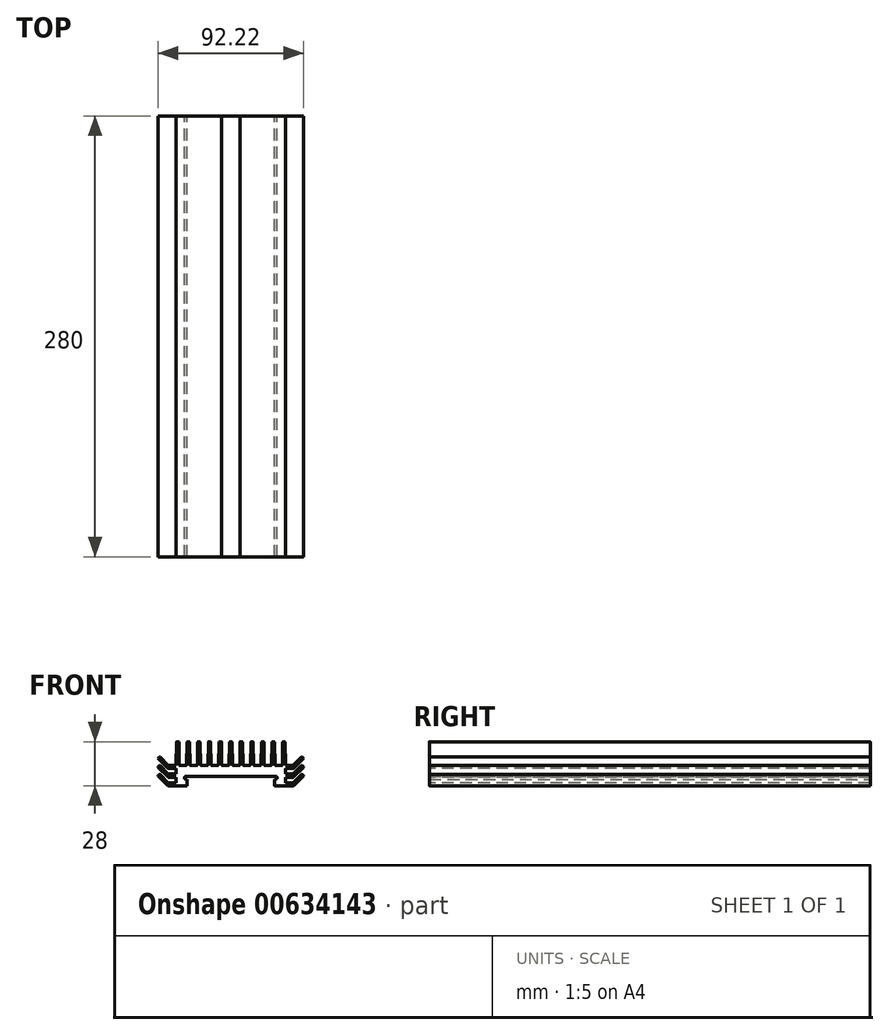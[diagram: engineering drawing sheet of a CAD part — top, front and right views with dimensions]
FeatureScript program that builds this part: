
annotation { "Feature Type Name" : "Feature", "Feature Type Description" : "" }
export const myFeature = defineFeature(function(context is Context, id is Id, definition is map)
    precondition{}
    {
        {
            var Q0;
            Q0=qCreatedBy(makeId("Front.planeOp"),FACE);
            var sketch = newSketch(context, id + "F0", { "sketchPlane" : qUnion([Q0])});
            skLineSegment(sketch, "E0.1.0.0", {"start": v(-33, 18.3) * mm, "end": v(-32.75, 3.7) * mm});
            skLineSegment(sketch, "E0.1.0.1", {"start": v(-32.55, 3.5) * mm, "end": v(-28.2, 3.5) * mm});
            skLineSegment(sketch, "E0.1.0.2", {"start": v(-34.75, 3.77) * mm, "end": v(-34.5, 18.3) * mm});
            skLineSegment(sketch, "E0.1.0.3", {"start": v(-34.3, 18.5) * mm, "end": v(-33.2, 18.5) * mm});
            skLineSegment(sketch, "E0.2.0.0", {"start": v(-26.25, 18.3) * mm, "end": v(-26, 3.7) * mm});
            skLineSegment(sketch, "E0.2.0.1", {"start": v(-25.8, 3.5) * mm, "end": v(-21.45, 3.5) * mm});
            skLineSegment(sketch, "E0.2.0.2", {"start": v(-28, 3.7) * mm, "end": v(-27.75, 18.3) * mm});
            skLineSegment(sketch, "E0.2.0.3", {"start": v(-27.55, 18.5) * mm, "end": v(-26.45, 18.5) * mm});
            skLineSegment(sketch, "E0.3.0.0", {"start": v(-19.5, 18.3) * mm, "end": v(-19.25, 3.7) * mm});
            skLineSegment(sketch, "E0.3.0.1", {"start": v(-19.05, 3.5) * mm, "end": v(-14.7, 3.5) * mm});
            skLineSegment(sketch, "E0.3.0.2", {"start": v(-21.25, 3.7) * mm, "end": v(-21, 18.3) * mm});
            skLineSegment(sketch, "E0.3.0.3", {"start": v(-20.8, 18.5) * mm, "end": v(-19.7, 18.5) * mm});
            skLineSegment(sketch, "E0.4.0.0", {"start": v(-12.75, 18.3) * mm, "end": v(-12.5, 3.7) * mm});
            skLineSegment(sketch, "E0.4.0.1", {"start": v(-12.3, 3.5) * mm, "end": v(-7.95, 3.5) * mm});
            skLineSegment(sketch, "E0.4.0.2", {"start": v(-14.5, 3.7) * mm, "end": v(-14.25, 18.3) * mm});
            skLineSegment(sketch, "E0.4.0.3", {"start": v(-14.05, 18.5) * mm, "end": v(-12.95, 18.5) * mm});
            skLineSegment(sketch, "E0.5.0.0", {"start": v(-5.75, 18.3) * mm, "end": v(-5.75, 3.7) * mm});
            skLineSegment(sketch, "E0.5.0.1", {"start": v(-5.55, 3.5) * mm, "end": v(-1.2, 3.5) * mm});
            skLineSegment(sketch, "E0.5.0.2", {"start": v(-7.75, 3.7) * mm, "end": v(-7.5, 18.3) * mm});
            skLineSegment(sketch, "E0.5.0.3", {"start": v(-7.3, 18.5) * mm, "end": v(-5.95, 18.5) * mm});
            skLineSegment(sketch, "E1.6.6.0", {"start": v(-1, 3.7) * mm, "end": v(-0.75, 18.3) * mm});
            skLineSegment(sketch, "E1.9.6.0", {"start": v(-0.55, 18.5) * mm, "end": v(0, 18.5) * mm});
            skPoint(sketch, "E2", {"position": v(0, 18.5) * mm});
            skPoint(sketch, "E3.visualSharp", {"position": v(-34.5, 18.5) * mm});
            skArc(sketch, "E3.filletArc", {"start": v(-34.3, 18.5) * mm, "mid": v(-34.44, 18.44) * mm, "end": v(-34.5, 18.3) * mm});
            skPoint(sketch, "E4.visualSharp", {"position": v(-33, 18.5) * mm});
            skArc(sketch, "E4.filletArc", {"start": v(-33, 18.3) * mm, "mid": v(-33.06, 18.44) * mm, "end": v(-33.2, 18.5) * mm});
            skPoint(sketch, "E5.visualSharp", {"position": v(-27.75, 18.5) * mm});
            skArc(sketch, "E5.filletArc", {"start": v(-27.55, 18.5) * mm, "mid": v(-27.7, 18.44) * mm, "end": v(-27.75, 18.3) * mm});
            skPoint(sketch, "E6.visualSharp", {"position": v(-26.25, 18.5) * mm});
            skArc(sketch, "E6.filletArc", {"start": v(-26.25, 18.3) * mm, "mid": v(-26.3, 18.44) * mm, "end": v(-26.45, 18.5) * mm});
            skPoint(sketch, "E7.visualSharp", {"position": v(-21, 18.5) * mm});
            skArc(sketch, "E7.filletArc", {"start": v(-20.8, 18.5) * mm, "mid": v(-20.94, 18.44) * mm, "end": v(-21, 18.3) * mm});
            skPoint(sketch, "E8.visualSharp", {"position": v(-19.5, 18.5) * mm});
            skArc(sketch, "E8.filletArc", {"start": v(-19.5, 18.3) * mm, "mid": v(-19.56, 18.44) * mm, "end": v(-19.7, 18.5) * mm});
            skPoint(sketch, "E9.visualSharp", {"position": v(-14.25, 18.5) * mm});
            skArc(sketch, "E9.filletArc", {"start": v(-14.05, 18.5) * mm, "mid": v(-14.2, 18.44) * mm, "end": v(-14.25, 18.3) * mm});
            skPoint(sketch, "E10.visualSharp", {"position": v(-12.75, 18.5) * mm});
            skArc(sketch, "E10.filletArc", {"start": v(-12.75, 18.3) * mm, "mid": v(-12.8, 18.44) * mm, "end": v(-12.95, 18.5) * mm});
            skPoint(sketch, "E11.visualSharp", {"position": v(-7.5, 18.5) * mm});
            skArc(sketch, "E11.filletArc", {"start": v(-7.3, 18.5) * mm, "mid": v(-7.44, 18.44) * mm, "end": v(-7.5, 18.3) * mm});
            skPoint(sketch, "E12.visualSharp", {"position": v(-5.75, 18.5) * mm});
            skArc(sketch, "E12.filletArc", {"start": v(-5.75, 18.3) * mm, "mid": v(-5.8, 18.44) * mm, "end": v(-5.95, 18.5) * mm});
            skPoint(sketch, "E13.visualSharp", {"position": v(-0.75, 18.5) * mm});
            skArc(sketch, "E13.filletArc", {"start": v(-0.55, 18.5) * mm, "mid": v(-0.7, 18.44) * mm, "end": v(-0.75, 18.3) * mm});
            skPoint(sketch, "E14.visualSharp", {"position": v(0, -3.5) * mm});
            skPoint(sketch, "E15.visualSharp", {"position": v(-32.75, 3.5) * mm});
            skArc(sketch, "E15.filletArc", {"start": v(-32.75, 3.7) * mm, "mid": v(-32.7, 3.56) * mm, "end": v(-32.55, 3.5) * mm});
            skPoint(sketch, "E16.visualSharp", {"position": v(-28, 3.5) * mm});
            skArc(sketch, "E16.filletArc", {"start": v(-28.2, 3.5) * mm, "mid": v(-28.06, 3.56) * mm, "end": v(-28, 3.7) * mm});
            skPoint(sketch, "E17.visualSharp", {"position": v(-26, 3.5) * mm});
            skArc(sketch, "E17.filletArc", {"start": v(-26, 3.7) * mm, "mid": v(-25.94, 3.56) * mm, "end": v(-25.8, 3.5) * mm});
            skPoint(sketch, "E18.visualSharp", {"position": v(-21.25, 3.5) * mm});
            skArc(sketch, "E18.filletArc", {"start": v(-21.45, 3.5) * mm, "mid": v(-21.3, 3.56) * mm, "end": v(-21.25, 3.7) * mm});
            skPoint(sketch, "E19.visualSharp", {"position": v(-19.25, 3.5) * mm});
            skArc(sketch, "E19.filletArc", {"start": v(-19.25, 3.7) * mm, "mid": v(-19.2, 3.56) * mm, "end": v(-19.05, 3.5) * mm});
            skPoint(sketch, "E20.visualSharp", {"position": v(-14.5, 3.5) * mm});
            skArc(sketch, "E20.filletArc", {"start": v(-14.7, 3.5) * mm, "mid": v(-14.56, 3.56) * mm, "end": v(-14.5, 3.7) * mm});
            skPoint(sketch, "E21.visualSharp", {"position": v(-12.5, 3.5) * mm});
            skArc(sketch, "E21.filletArc", {"start": v(-12.5, 3.7) * mm, "mid": v(-12.44, 3.56) * mm, "end": v(-12.3, 3.5) * mm});
            skPoint(sketch, "E22.visualSharp", {"position": v(-7.75, 3.5) * mm});
            skArc(sketch, "E22.filletArc", {"start": v(-7.95, 3.5) * mm, "mid": v(-7.8, 3.56) * mm, "end": v(-7.75, 3.7) * mm});
            skPoint(sketch, "E23.visualSharp", {"position": v(-5.75, 3.5) * mm});
            skArc(sketch, "E23.filletArc", {"start": v(-5.75, 3.7) * mm, "mid": v(-5.7, 3.56) * mm, "end": v(-5.55, 3.5) * mm});
            skPoint(sketch, "E24.visualSharp", {"position": v(-1, 3.5) * mm});
            skArc(sketch, "E24.filletArc", {"start": v(-1.2, 3.5) * mm, "mid": v(-1.06, 3.56) * mm, "end": v(-1, 3.7) * mm});
            skLineSegment(sketch, "E25", {"start": v(-27.75, -5.25) * mm, "end": v(-27.75, -9.3) * mm});
            skPoint(sketch, "E26.visualSharp", {"position": v(-27.75, -9.5) * mm});
            skArc(sketch, "E26.filletArc", {"start": v(-27.95, -9.5) * mm, "mid": v(-27.8, -9.44) * mm, "end": v(-27.75, -9.3) * mm});
            skLineSegment(sketch, "E27", {"start": v(-34.75, 3.77) * mm, "end": v(-34.75, -9.5) * mm});
            skLineSegment(sketch, "E28", {"start": v(-27.95, -9.5) * mm, "end": v(-34.75, -9.5) * mm});
            skLineSegment(sketch, "E29", {"start": v(0, 18.5) * mm, "end": v(0, -3.5) * mm});
            skLineSegment(sketch, "E30.bottom", {"start": v(-27.75, -5.25) * mm, "end": v(-28.62, -5.25) * mm});
            skArc(sketch, "E31", {"start": v(-28.62, -3.5) * mm, "mid": v(-29.5, -4.38) * mm, "end": v(-28.62, -5.25) * mm});
            skPoint(sketch, "E32", {"position": v(-29.5, -4.38) * mm});
            skLineSegment(sketch, "E33", {"start": v(-28.62, -3.5) * mm, "end": v(0, -3.5) * mm});
            skSolve(sketch);
        }
        {
            var Q0;
            Q0=qSketchRegion(id+"F0",true);
            extrude(context, id + "F1", {"entities" : qUnion([Q0]), "depth" : 280 * mm, "offsetDistance" : 25 * mm});
        }
        {
            var Q0;
            Q0=makeQuery(id+"F1.opExtrude","CAP_FACE",FACE,{"disambiguationData":[OSD([sQuery(id+"F0.wireOp",EDGE,"bL3qZI64-7qrA-8tBo-xELN-WwCQw7n5xeQu"),sQuery(id+"F0.wireOp",EDGE,"nefEkcPL-9hmu-xnLm-Q7lG-tzpoaju1hbQN"),sQuery(id+"F0.wireOp",EDGE,"E0.1.0.0"),sQuery(id+"F0.wireOp",EDGE,"E0.1.0.1"),sQuery(id+"F0.wireOp",EDGE,"E0.1.0.2"),sQuery(id+"F0.wireOp",EDGE,"E0.1.0.3"),sQuery(id+"F0.wireOp",EDGE,"E0.2.0.0"),sQuery(id+"F0.wireOp",EDGE,"E0.2.0.1"),sQuery(id+"F0.wireOp",EDGE,"E0.2.0.2"),sQuery(id+"F0.wireOp",EDGE,"E0.2.0.3"),sQuery(id+"F0.wireOp",EDGE,"E0.3.0.0"),sQuery(id+"F0.wireOp",EDGE,"E0.3.0.1"),sQuery(id+"F0.wireOp",EDGE,"E0.3.0.2"),sQuery(id+"F0.wireOp",EDGE,"E0.3.0.3"),sQuery(id+"F0.wireOp",EDGE,"E0.4.0.0"),sQuery(id+"F0.wireOp",EDGE,"E0.4.0.1"),sQuery(id+"F0.wireOp",EDGE,"E0.4.0.2"),sQuery(id+"F0.wireOp",EDGE,"E0.4.0.3"),sQuery(id+"F0.wireOp",EDGE,"E0.5.0.0"),sQuery(id+"F0.wireOp",EDGE,"E0.5.0.1"),sQuery(id+"F0.wireOp",EDGE,"E0.5.0.2"),sQuery(id+"F0.wireOp",EDGE,"E0.5.0.3"),sQuery(id+"F0.wireOp",EDGE,"E1.6.6.0"),sQuery(id+"F0.wireOp",EDGE,"E1.9.6.0"),sQuery(id+"F0.wireOp",EDGE,"cGjzFalO-vpqR-JREd-c4S5-U7nG7IJ00PFV"),sQuery(id+"F0.wireOp",EDGE,"zfFNARTa-EHTY-tQI5-zIkq-Cr7m6sKq9WCR"),sQuery(id+"F0.wireOp",EDGE,"KjC3TMZQ-COVc-rKvV-FkOu-ZatDV2PMTpZc"),sQuery(id+"F0.wireOp",EDGE,"mlO0Lyb2-eVYo-AatF-SlvP-83DAQH0pbuAu"),sQuery(id+"F0.wireOp",EDGE,"E3.filletArc"),sQuery(id+"F0.wireOp",EDGE,"E4.filletArc"),sQuery(id+"F0.wireOp",EDGE,"E5.filletArc"),sQuery(id+"F0.wireOp",EDGE,"E6.filletArc"),sQuery(id+"F0.wireOp",EDGE,"E7.filletArc"),sQuery(id+"F0.wireOp",EDGE,"E8.filletArc"),sQuery(id+"F0.wireOp",EDGE,"E9.filletArc"),sQuery(id+"F0.wireOp",EDGE,"E10.filletArc"),sQuery(id+"F0.wireOp",EDGE,"E11.filletArc"),sQuery(id+"F0.wireOp",EDGE,"E12.filletArc"),sQuery(id+"F0.wireOp",EDGE,"E13.filletArc"),sQuery(id+"F0.wireOp",EDGE,"f700f213-2786-48f4-a4ca-97d2954a505b.filletArc"),sQuery(id+"F0.wireOp",EDGE,"ee50963b-3f6e-45a6-9550-016bf928bd64.filletArc"),sQuery(id+"F0.wireOp",EDGE,"3fa5c7a0-46de-4f7c-b7f0-d3e079dab4d4.filletArc"),sQuery(id+"F0.wireOp",EDGE,"1a05ea91-b8e8-4e60-8976-cabcb86d6e5d.filletArc"),sQuery(id+"F0.wireOp",EDGE,"4ed3edbc-86c1-4c2d-b3db-7962da8c7f3b.filletArc"),sQuery(id+"F0.wireOp",EDGE,"df53fec7-61cd-4923-a6ae-b9e3b851a0f2.filletArc"),sQuery(id+"F0.wireOp",EDGE,"E15.filletArc"),sQuery(id+"F0.wireOp",EDGE,"E16.filletArc"),sQuery(id+"F0.wireOp",EDGE,"E17.filletArc"),sQuery(id+"F0.wireOp",EDGE,"E18.filletArc"),sQuery(id+"F0.wireOp",EDGE,"E19.filletArc"),sQuery(id+"F0.wireOp",EDGE,"E20.filletArc"),sQuery(id+"F0.wireOp",EDGE,"E21.filletArc"),sQuery(id+"F0.wireOp",EDGE,"E22.filletArc"),sQuery(id+"F0.wireOp",EDGE,"E23.filletArc"),sQuery(id+"F0.wireOp",EDGE,"E24.filletArc"),sQuery(id+"F0.wireOp",EDGE,"hxUGQoIj-TBv8-McRq-7C4Q-voeCxAJpT5fA"),sQuery(id+"F0.wireOp",EDGE,"4HJRwaON-CD5F-kCda-4T6D-As3IOU8s3CqO"),sQuery(id+"F0.wireOp",EDGE,"uo7RkyCL-c98j-zEhM-1sWP-hJWaIm8JIuHS"),sQuery(id+"F0.wireOp",EDGE,"UyrvhKvo-Hriy-DGAL-Pid4-MuuIVOQ2I04g"),sQuery(id+"F0.wireOp",EDGE,"U6ICKPt3-iNcd-rmJ2-pTeO-fHKRQgZmkzro"),sQuery(id+"F0.wireOp",EDGE,"cJHcNlIk-0kYQ-5AfO-mOoR-XwhJbZEzOTLT"),sQuery(id+"F0.wireOp",EDGE,"E25"),sQuery(id+"F0.wireOp",EDGE,"E26.filletArc"),sQuery(id+"F0.wireOp",EDGE,"1ba531c4-4689-4158-b5fc-088271326b5e.filletArc"),sQuery(id+"F0.wireOp",EDGE,"e30eec23-a2ac-48d1-9385-250101e62e32.filletArc")])],"isStart":false});
            var sketch = newSketch(context, id + "F2", { "sketchPlane" : qUnion([Q0])});
            skLineSegment(sketch, "E34", {"start": v(-34.75, -7.5) * mm, "end": v(-39.54, -7.5) * mm});
            skLineSegment(sketch, "E35", {"start": v(-34.75, -9.5) * mm, "end": v(-39.75, -9.5) * mm});
            skLineSegment(sketch, "E36", {"start": v(-39.68, -7.45) * mm, "end": v(-45, -2.13) * mm});
            skLineSegment(sketch, "E37", {"start": v(-39.8, -9.44) * mm, "end": v(-46.06, -3.19) * mm});
            skLineSegment(sketch, "E38", {"start": v(-45.28, -2.13) * mm, "end": v(-46.06, -2.9) * mm});
            skLineSegment(sketch, "E39", {"start": v(-34.75, -7.5) * mm, "end": v(-34.75, -9.5) * mm});
            skLineSegment(sketch, "E40.direction2", {"start": v(-39.75, -9.5) * mm, "end": v(-39.75, -4) * mm, "construction": true});
            skPoint(sketch, "E41.visualSharp", {"position": v(-39.62, -7.5) * mm});
            skArc(sketch, "E41.filletArc", {"start": v(-39.68, -7.45) * mm, "mid": v(-39.61, -7.49) * mm, "end": v(-39.54, -7.5) * mm});
            skPoint(sketch, "E42.visualSharp", {"position": v(-45.14, -1.99) * mm});
            skArc(sketch, "E42.filletArc", {"start": v(-45, -2.13) * mm, "mid": v(-45.14, -2.07) * mm, "end": v(-45.28, -2.13) * mm});
            skPoint(sketch, "E43.visualSharp", {"position": v(-46.2, -3.05) * mm});
            skArc(sketch, "E43.filletArc", {"start": v(-46.06, -2.9) * mm, "mid": v(-46.11, -3.05) * mm, "end": v(-46.06, -3.19) * mm});
            skPoint(sketch, "E44.visualSharp", {"position": v(-39.75, -9.5) * mm});
            skArc(sketch, "E44.filletArc", {"start": v(-39.8, -9.44) * mm, "mid": v(-39.74, -9.48) * mm, "end": v(-39.66, -9.5) * mm});
            skLineSegment(sketch, "E45.0.1.0", {"start": v(-34.75, -2) * mm, "end": v(-34.75, -4) * mm});
            skLineSegment(sketch, "E45.0.1.1", {"start": v(-39.75, -4) * mm, "end": v(-39.75, 1.5) * mm, "construction": true});
            skPoint(sketch, "E45.0.1.2", {"position": v(-46.2, 2.45) * mm});
            skLineSegment(sketch, "E45.0.1.3", {"start": v(-39.8, -3.94) * mm, "end": v(-46.06, 2.31) * mm});
            skLineSegment(sketch, "E45.0.1.4", {"start": v(-34.75, -2) * mm, "end": v(-39.54, -2) * mm});
            skLineSegment(sketch, "E45.0.1.5", {"start": v(-34.75, -4) * mm, "end": v(-39.75, -4) * mm});
            skPoint(sketch, "E45.0.1.6", {"position": v(-45.14, 3.51) * mm});
            skPoint(sketch, "E45.0.1.7", {"position": v(-39.62, -2) * mm});
            skLineSegment(sketch, "E45.0.1.8", {"start": v(-39.68, -1.95) * mm, "end": v(-45, 3.37) * mm});
            skPoint(sketch, "E45.0.1.9", {"position": v(-39.75, -4) * mm});
            skLineSegment(sketch, "E45.0.1.10", {"start": v(-45.28, 3.37) * mm, "end": v(-46.06, 2.6) * mm});
            skArc(sketch, "E45.0.1.11", {"start": v(-46.06, 2.6) * mm, "mid": v(-46.11, 2.45) * mm, "end": v(-46.06, 2.31) * mm});
            skArc(sketch, "E45.0.1.12", {"start": v(-45, 3.37) * mm, "mid": v(-45.14, 3.43) * mm, "end": v(-45.28, 3.37) * mm});
            skArc(sketch, "E45.0.1.13", {"start": v(-39.68, -1.95) * mm, "mid": v(-39.61, -1.99) * mm, "end": v(-39.54, -2) * mm});
            skArc(sketch, "E45.0.1.14", {"start": v(-39.8, -3.94) * mm, "mid": v(-39.74, -3.98) * mm, "end": v(-39.66, -4) * mm});
            skLineSegment(sketch, "E45.0.2.0", {"start": v(-34.75, 3.5) * mm, "end": v(-34.75, 1.5) * mm});
            skLineSegment(sketch, "E45.0.2.1", {"start": v(-39.75, 1.5) * mm, "end": v(-39.75, 7) * mm, "construction": true});
            skPoint(sketch, "E45.0.2.2", {"position": v(-46.2, 7.95) * mm});
            skLineSegment(sketch, "E45.0.2.3", {"start": v(-39.8, 1.56) * mm, "end": v(-46.06, 7.81) * mm});
            skLineSegment(sketch, "E45.0.2.4", {"start": v(-34.75, 3.5) * mm, "end": v(-39.54, 3.5) * mm});
            skLineSegment(sketch, "E45.0.2.5", {"start": v(-34.75, 1.5) * mm, "end": v(-39.75, 1.5) * mm});
            skPoint(sketch, "E45.0.2.6", {"position": v(-45.14, 9.01) * mm});
            skPoint(sketch, "E45.0.2.7", {"position": v(-39.62, 3.5) * mm});
            skLineSegment(sketch, "E45.0.2.8", {"start": v(-39.68, 3.55) * mm, "end": v(-45, 8.87) * mm});
            skPoint(sketch, "E45.0.2.9", {"position": v(-39.75, 1.5) * mm});
            skLineSegment(sketch, "E45.0.2.10", {"start": v(-45.28, 8.87) * mm, "end": v(-46.06, 8.1) * mm});
            skArc(sketch, "E45.0.2.11", {"start": v(-46.06, 8.1) * mm, "mid": v(-46.11, 7.95) * mm, "end": v(-46.06, 7.81) * mm});
            skArc(sketch, "E45.0.2.12", {"start": v(-45, 8.87) * mm, "mid": v(-45.14, 8.93) * mm, "end": v(-45.28, 8.87) * mm});
            skArc(sketch, "E45.0.2.13", {"start": v(-39.68, 3.55) * mm, "mid": v(-39.61, 3.51) * mm, "end": v(-39.54, 3.5) * mm});
            skArc(sketch, "E45.0.2.14", {"start": v(-39.8, 1.56) * mm, "mid": v(-39.74, 1.52) * mm, "end": v(-39.66, 1.5) * mm});
            skLineSegment(sketch, "E45.direction1", {"start": v(-39.75, -9.5) * mm, "end": v(-14.75, -9.5) * mm, "construction": true});
            skSolve(sketch);
        }
        {
            var Q0;
            Q0=qSketchRegion(id+"F2",true);
            extrude(context, id + "F3", {"entities" : qUnion([Q0]), "operationType" : NewBodyOperationType.ADD, "oppositeDirection" : true, "depth" : 280 * mm, "offsetDistance" : 25 * mm});
        }
        {
            var Q0;
            Q0=makeQuery(id+"F1.opExtrude","SWEPT_BODY",BODY,{"disambiguationData":[OSD([sQuery(id+"F0.wireOp",EDGE,"QOM90pkH-KK3E-2t4G-PR0d-VXwYNY4fjtTb"),sQuery(id+"F0.wireOp",EDGE,"Wt8m1K6G-Pg8W-yz88-BKp3-o8GU5yjb4NPO"),sQuery(id+"F0.wireOp",EDGE,"F3vcOgBq-LlWr-xvjw-e04Y-niSAJOFfG4p2"),sQuery(id+"F0.wireOp",EDGE,"u1mY0JJN-f7Kk-nBfH-W6HL-n9qIg2MDpbPP"),sQuery(id+"F0.wireOp",EDGE,"QIDlm4V3-j7gJ-oFi3-cvUC-kSezUPiWFmIS"),sQuery(id+"F0.wireOp",EDGE,"6xrvO9A8-pm1h-AeFb-QTYX-2HOc3FF3rfEQ"),sQuery(id+"F0.wireOp",EDGE,"Nf9yDHwn-gt6s-M4IA-LLNt-3061gzFxuUBp"),sQuery(id+"F0.wireOp",EDGE,"WuwbFeWC-LNyf-1R1Z-RHmS-f9KyMF8TMt9i"),sQuery(id+"F0.wireOp",EDGE,"UM4JaTJU-Vk1M-XgEN-ImDx-eCgJd49Y6FMu"),sQuery(id+"F0.wireOp",EDGE,"OvlMNyBG-IFKC-w7DX-ZWVS-3YzXS4CVPNQT"),sQuery(id+"F0.wireOp",EDGE,"jmIuwl2N-ih4h-DjTB-hYCO-kHODNnBOpXJs"),sQuery(id+"F0.wireOp",EDGE,"bhDqv4Mq-hX6j-4xH4-fuLw-w89xF4HoMTrF"),sQuery(id+"F0.wireOp",EDGE,"bL3qZI64-7qrA-8tBo-xELN-WwCQw7n5xeQu"),sQuery(id+"F0.wireOp",EDGE,"nefEkcPL-9hmu-xnLm-Q7lG-tzpoaju1hbQN"),sQuery(id+"F0.wireOp",EDGE,"DATJw4Rr-6OHI-e9sL-mig8-pdpoUj6XXJZJ"),sQuery(id+"F0.wireOp",EDGE,"ed90f767-a289-48e3-8617-8c3c22fb4d72.trimOffspring"),sQuery(id+"F0.wireOp",EDGE,"7ho3JKrC-G9q0-DxLB-qz2V-eUSqsKLsZmBJ"),sQuery(id+"F0.wireOp",EDGE,"Nb5lTvUm-lXxh-YIyg-5x1b-LZ3tmgTk2abY"),sQuery(id+"F0.wireOp",EDGE,"Z2SCv61l-lqp3-au7K-zo4L-WJUViGbaLhYw"),sQuery(id+"F0.wireOp",EDGE,"qlelKb4N-GS20-CHXp-tJnn-sWviO8Gk2iGX"),sQuery(id+"F0.wireOp",EDGE,"E0.1.0.0"),sQuery(id+"F0.wireOp",EDGE,"E0.1.0.1"),sQuery(id+"F0.wireOp",EDGE,"E0.1.0.2"),sQuery(id+"F0.wireOp",EDGE,"E0.1.0.3"),sQuery(id+"F0.wireOp",EDGE,"E0.2.0.0"),sQuery(id+"F0.wireOp",EDGE,"E0.2.0.1"),sQuery(id+"F0.wireOp",EDGE,"E0.2.0.2"),sQuery(id+"F0.wireOp",EDGE,"E0.2.0.3"),sQuery(id+"F0.wireOp",EDGE,"E0.3.0.0"),sQuery(id+"F0.wireOp",EDGE,"E0.3.0.1"),sQuery(id+"F0.wireOp",EDGE,"E0.3.0.2"),sQuery(id+"F0.wireOp",EDGE,"E0.3.0.3"),sQuery(id+"F0.wireOp",EDGE,"E0.4.0.0"),sQuery(id+"F0.wireOp",EDGE,"E0.4.0.1"),sQuery(id+"F0.wireOp",EDGE,"E0.4.0.2"),sQuery(id+"F0.wireOp",EDGE,"E0.4.0.3"),sQuery(id+"F0.wireOp",EDGE,"E0.5.0.0"),sQuery(id+"F0.wireOp",EDGE,"E0.5.0.1"),sQuery(id+"F0.wireOp",EDGE,"E0.5.0.2"),sQuery(id+"F0.wireOp",EDGE,"E0.5.0.3"),sQuery(id+"F0.wireOp",EDGE,"E1.6.6.0"),sQuery(id+"F0.wireOp",EDGE,"E1.9.6.0"),sQuery(id+"F0.wireOp",EDGE,"yGFb3Jfo-Lhlh-xzfz-Ljs9-34xcXF1H7Gp1"),sQuery(id+"F0.wireOp",EDGE,"dxc8wIRG-n3ac-7oqY-UQSt-FR4flQWY79jH"),sQuery(id+"F0.wireOp",EDGE,"pMfyub31-Xo22-kmQh-hgcO-EaUa3d53Z9ym"),sQuery(id+"F0.wireOp",EDGE,"EXS0VTzR-uZRH-gpkk-ciJv-APifiNII5ex7"),sQuery(id+"F0.wireOp",EDGE,"j9COY3aO-4lFf-zBAU-mgS4-eOpnypJtWWPn")])]});
            var Q1;
            Q1=makeQuery(id+"F1.opExtrude","SWEPT_FACE",FACE,{"disambiguationData":[OSD([sQuery(id+"F0.wireOp",EDGE,"E29")])]});
            mirror(context, id + "F4", {"operationType" : NewBodyOperationType.ADD, "entities" : qUnion([Q0]), "mirrorPlane" : qUnion([Q1])});
        }
    });
